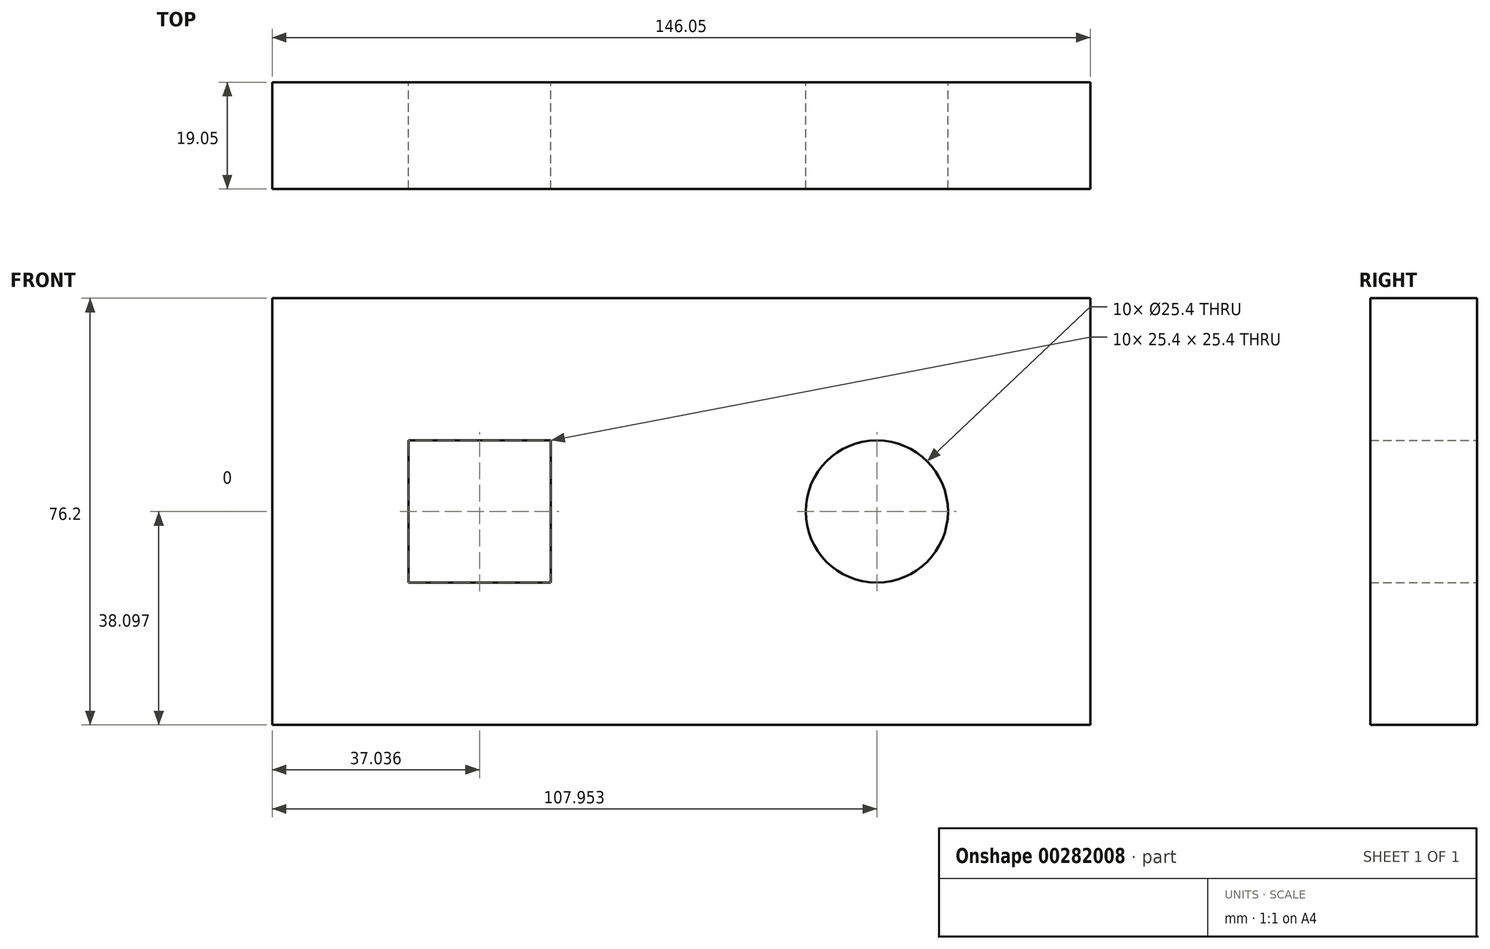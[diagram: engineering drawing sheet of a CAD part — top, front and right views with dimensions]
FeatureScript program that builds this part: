
annotation { "Feature Type Name" : "Feature", "Feature Type Description" : "" }
export const myFeature = defineFeature(function(context is Context, id is Id, definition is map)
    precondition{}
    {
        {
            var Q0;
            Q0=qCreatedBy(makeId("Front.planeOp"),FACE);
            var sketch = newSketch(context, id + "F0", { "sketchPlane" : qUnion([Q0])});
            skLineSegment(sketch, "E0.bottom", {"start": v(-69.48, 53.67) * mm, "end": v(76.57, 53.67) * mm});
            skLineSegment(sketch, "E0.top", {"start": v(-69.48, -22.53) * mm, "end": v(76.57, -22.53) * mm});
            skLineSegment(sketch, "E0.left", {"start": v(-69.48, 53.67) * mm, "end": v(-69.48, -22.53) * mm});
            skLineSegment(sketch, "E0.right", {"start": v(76.57, 53.67) * mm, "end": v(76.57, -22.53) * mm});
            skLineSegment(sketch, "E1.bottom", {"start": v(-19.74, 2.87) * mm, "end": v(-45.14, 2.87) * mm});
            skLineSegment(sketch, "E1.top", {"start": v(-19.74, 28.27) * mm, "end": v(-45.14, 28.27) * mm});
            skLineSegment(sketch, "E1.left", {"start": v(-19.74, 2.87) * mm, "end": v(-19.74, 28.27) * mm});
            skLineSegment(sketch, "E1.right", {"start": v(-45.14, 2.87) * mm, "end": v(-45.14, 28.27) * mm});
            skCircle(sketch, "E2", {"center": v(38.47, 15.57) * mm, "radius": 12.7 * mm});
            skSolve(sketch);
        }
        {
            var Q0;
            Q0=makeQuery(id+"F0.imprint","IMPRINT",FACE,{"disambiguationData":[TD([[makeQuery(id+"F0.imprint","IMPRINT",EDGE,{"derivedFrom":sQuery(id+"F0.wireOp",EDGE,"E0.bottom")}),-1.0]])]});
            extrude(context, id + "F1", {"entities" : qUnion([Q0]), "depth" : 19.05 * mm});
        }
    });
